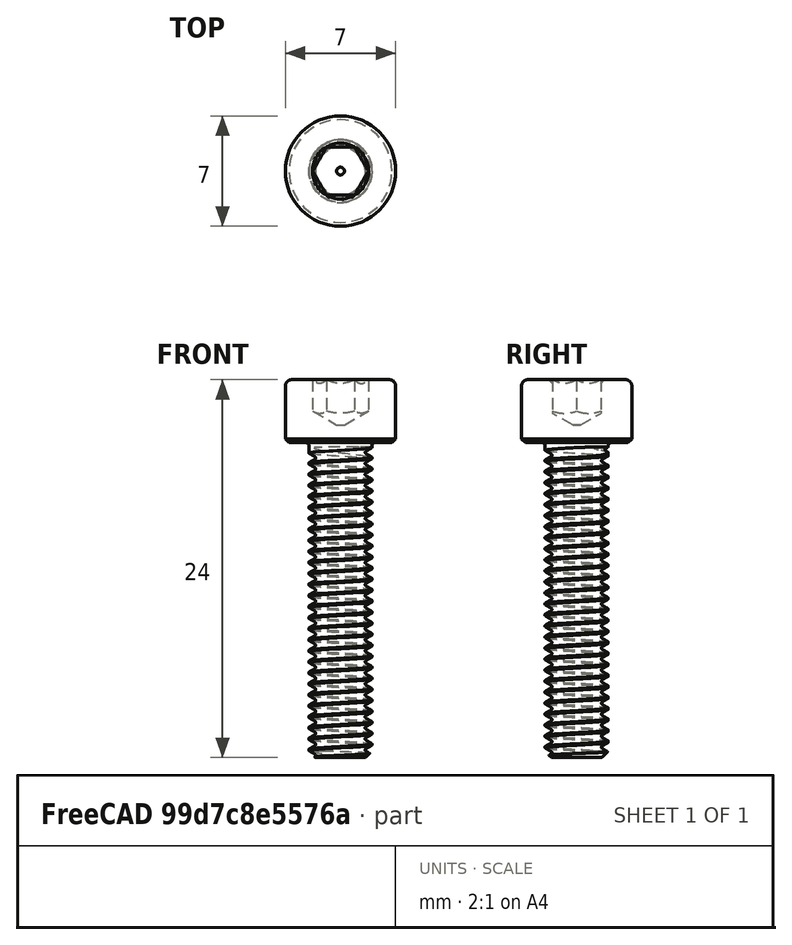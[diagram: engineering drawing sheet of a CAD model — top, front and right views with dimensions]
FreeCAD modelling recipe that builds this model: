
FCSTD DOCUMENT  (FreeCAD 2023.521R14555 (Git shallow))
Label: M4x20
License: All rights reserved
LicenseURL: http://en.wikipedia.org/wiki/All_rights_reserved
objects: Part::FeaturePython×4, App::AnnotationLabel×2, PartDesign::CoordinateSystem×1, App::Part×1, App::DocumentObjectGroup×1
note: 5 computed .brp shape members not serialized (recipe doc carries the construction recipe); baked Part::Feature solids carry a one-line shape summary decoded from their .brp

FEATURE [Part::FeaturePython] Screw  label="M4x20-Screw"  # Fasteners workbench fastener (typed FeaturePython)
  InvalidShape = false
  TreeRank = 0
  ValidateShape = false
  diameter = 5
  invert = false
  leftHanded = false
  length = 6
  lengthCustom = 20
  matchOuter = false
  offset = 0
  thread = true
  type = 45
FEATURE [PartDesign::CoordinateSystem] LCS_1
  AttacherType = Attacher::AttachEngine3D
  AttachmentSupport = -> [Screw]
  InvalidShape = false
  MapMode = 11
  Placement = pos=(0,0,0) rot=(0.707107,-0.707107,0;3.14159rad)
  Support = -> [Screw]
  TreeRank = 0
  ValidateShape = false
FEATURE [App::Part] M4
  ClaimAllChildren = false
  ExportMode = 1
  Group = -> [Screw,LCS_1]
  Origin = -> Origin
  TreeRank = 0
  _ExportChildren = -> [Screw,LCS_1]
  _GroupVersion = 1
FEATURE [Part::FeaturePython] aCircle  # WARN: FeaturePython — macro-defined, semantics opaque (R4)
  InvalidShape = false
  TreeRank = 5
  ValidateShape = false
FEATURE [Part::FeaturePython] Radius  # WARN: FeaturePython — macro-defined, semantics opaque (R4)
  InvalidShape = false
  TreeRank = 3
  ValidateShape = false
FEATURE [App::AnnotationLabel] MeasureLbl
  BasePosition = (3.5,0,3.6)
  LabelText = R = 3.50 mm
  TextPosition = (0,0,0)
  TreeRank = 4
FEATURE [Part::FeaturePython] DistPoints  # WARN: FeaturePython — macro-defined, semantics opaque (R4)
  InvalidShape = false
  TreeRank = 9
  ValidateShape = false
FEATURE [App::AnnotationLabel] MeasureLbl001
  BasePosition = (-1.88776,1e-16,1.9)
  LabelText = D = 4.21 mm
  TextPosition = (0,0,0)
  TreeRank = 10
FEATURE [App::DocumentObjectGroup] Measures
  ClaimAllChildren = true
  ExportMode = 1
  Group = -> [aCircle,Radius,MeasureLbl,DistPoints,MeasureLbl001]
  TreeRank = 6
  _GroupVersion = 1
